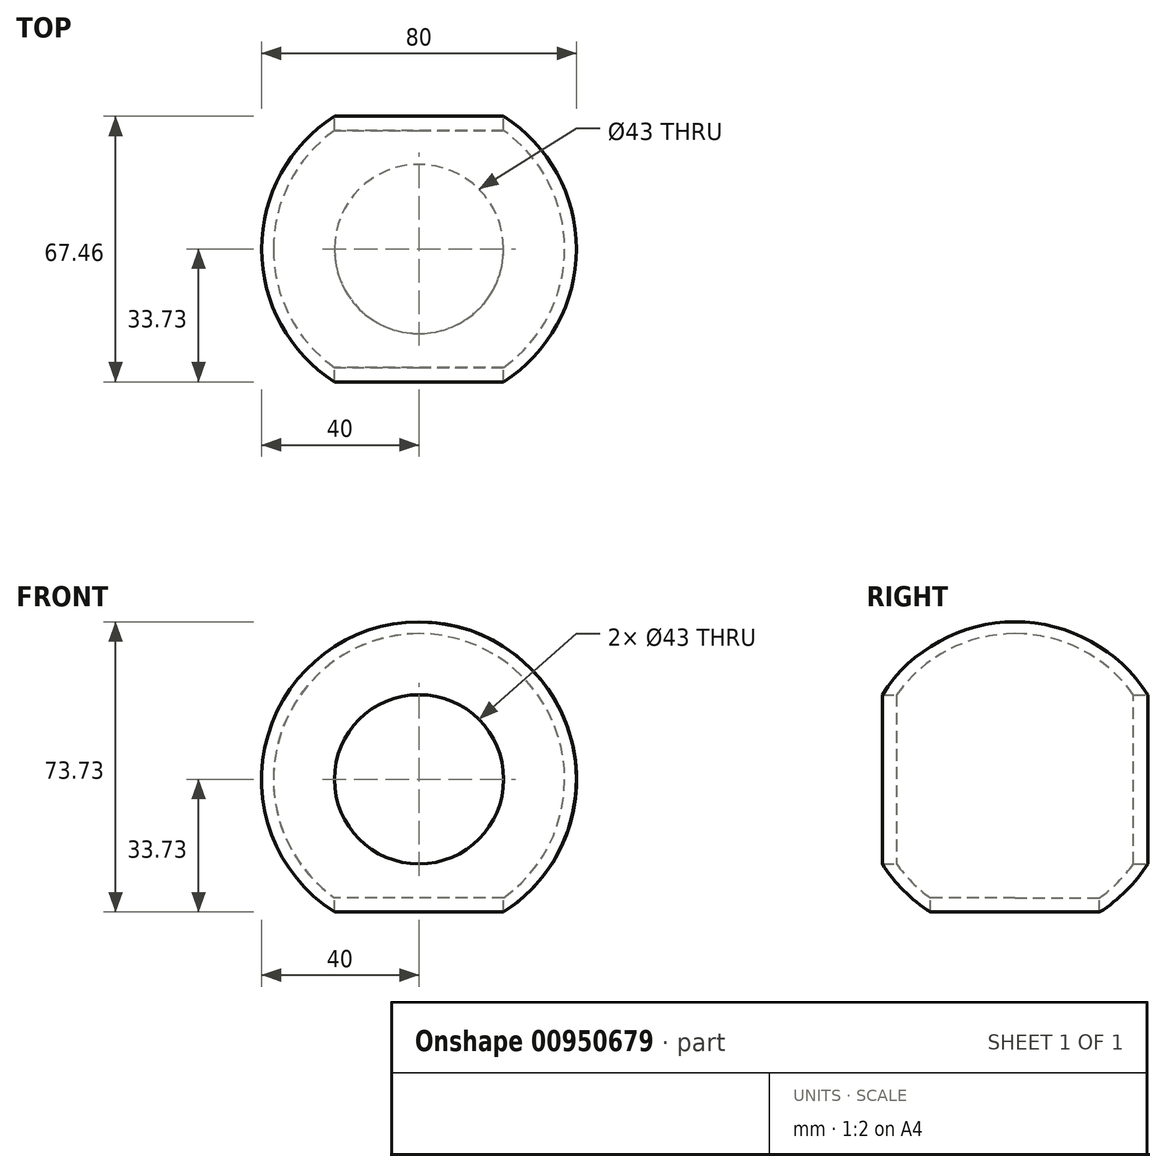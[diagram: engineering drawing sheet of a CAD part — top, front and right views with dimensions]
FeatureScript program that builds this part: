
annotation { "Feature Type Name" : "Feature", "Feature Type Description" : "" }
export const myFeature = defineFeature(function(context is Context, id is Id, definition is map)
    precondition{}
    {
        {
            var Q0;
            Q0=qCreatedBy(makeId("Front.planeOp"),FACE);
            var sketch = newSketch(context, id + "F0", { "sketchPlane" : qUnion([Q0])});
            skArc(sketch, "E0", {"start": v(0, 40) * mm, "mid": v(-40, 0) * mm, "end": v(0, -40) * mm});
            skArc(sketch, "E1", {"start": v(0, 37) * mm, "mid": v(-37, 0) * mm, "end": v(0, -37) * mm});
            skLineSegment(sketch, "E2", {"start": v(0, 37) * mm, "end": v(0, 40) * mm});
            skLineSegment(sketch, "E3", {"start": v(0, -37) * mm, "end": v(0, -40) * mm});
            skSolve(sketch);
        }
        {
            var Q0;
            Q0=makeQuery(id+"F0.imprint","IMPRINT",FACE,{"disambiguationData":[TD([[makeQuery(id+"F0.imprint","IMPRINT",EDGE,{"derivedFrom":sQuery(id+"F0.wireOp",EDGE,"E0")}),1.0]])]});
            var Q1;
            Q1=sQuery(id+"F0.wireOp",EDGE,"E3");
            revolve(context, id + "F1", {"surfaceOperationType" : NewSurfaceOperationType.NEW, "entities" : qUnion([Q0]), "axis" : qUnion([Q1]), "revolveType" : RevolveType.FULL, "oppositeDirection" : true});
        }
        {
            var Q0;
            Q0=qCreatedBy(makeId("Front.planeOp"),FACE);
            var sketch = newSketch(context, id + "F2", { "sketchPlane" : qUnion([Q0])});
            skCircle(sketch, "E4", {"center": v(0, 0) * mm, "radius": 21.5 * mm});
            skSolve(sketch);
        }
        {
            var Q0;
            Q0 = qSketchRegion(id + "F2", true);
            extrude(context, id + "F3", {"entities" : qUnion([Q0]), "operationType" : NewBodyOperationType.REMOVE, "flatOperationType" : FlatOperationType.REMOVE, "endBound" : BoundingType.THROUGH_ALL, "depth" : 25 * mm, "offsetDistance" : 25 * mm, "hasSecondDirection" : true, "secondDirectionBound" : BoundingType.THROUGH_ALL, "secondDirectionOppositeDirection" : true, "secondDirectionDepth" : 25 * mm, "domain" : OperationDomain.MODEL});
        }
        {
            var Q0;
            Q0=qCreatedBy(makeId("Top.planeOp"),FACE);
            var sketch = newSketch(context, id + "F4", { "sketchPlane" : qUnion([Q0])});
            skCircle(sketch, "E5", {"center": v(0, 0) * mm, "radius": 21.5 * mm});
            skSolve(sketch);
        }
        {
            var Q0;
            Q0 = qSketchRegion(id + "F4", true);
            extrude(context, id + "F5", {"entities" : qUnion([Q0]), "operationType" : NewBodyOperationType.REMOVE, "flatOperationType" : FlatOperationType.REMOVE, "endBound" : BoundingType.THROUGH_ALL, "oppositeDirection" : true, "depth" : 25 * mm, "offsetDistance" : 25 * mm, "domain" : OperationDomain.MODEL});
        }
    });
